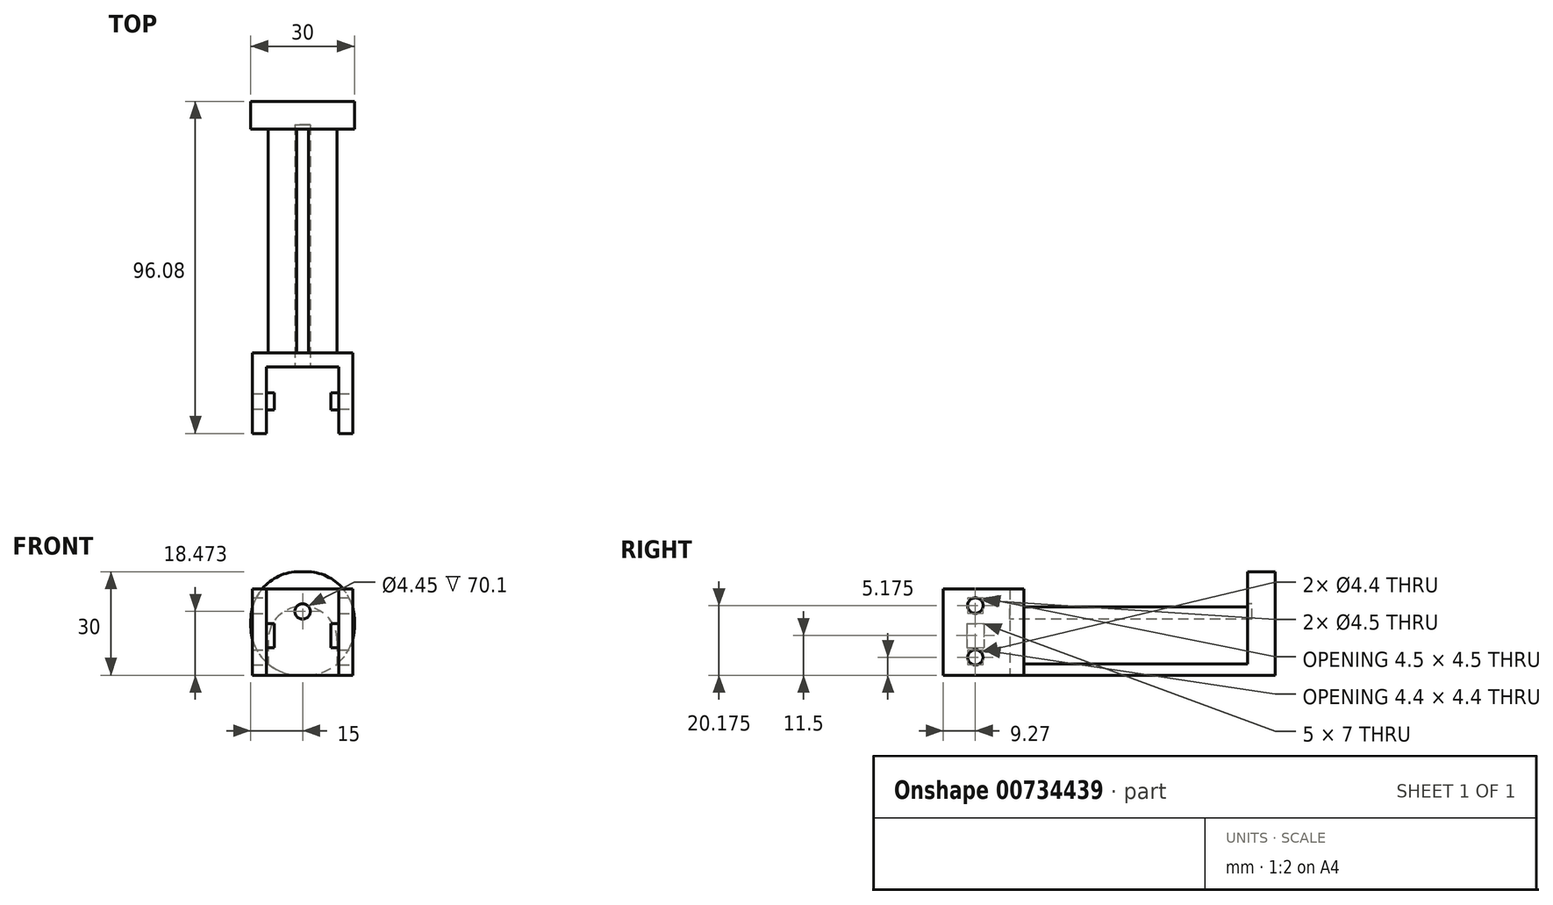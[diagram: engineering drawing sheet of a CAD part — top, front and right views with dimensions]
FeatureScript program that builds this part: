
annotation { "Feature Type Name" : "Feature", "Feature Type Description" : "" }
export const myFeature = defineFeature(function(context is Context, id is Id, definition is map)
    precondition{}
    {
        {
            var Q0;
            Q0=qCreatedBy(makeId("Top.planeOp"),FACE);
            var sketch = newSketch(context, id + "F0", { "sketchPlane" : qUnion([Q0])});
            skLineSegment(sketch, "E0.bottom", {"start": v(13.98, 2.5) * mm, "end": v(8.23, 2.5) * mm});
            skLineSegment(sketch, "E0.top", {"start": v(13.98, -2.5) * mm, "end": v(8.23, -2.5) * mm});
            skLineSegment(sketch, "E0.left", {"start": v(13.98, 2.5) * mm, "end": v(13.98, -2.5) * mm});
            skLineSegment(sketch, "E0.right", {"start": v(8.23, 2.5) * mm, "end": v(8.23, -2.5) * mm});
            skPoint(sketch, "E0.middle", {"position": v(11.1, 0) * mm});
            skPoint(sketch, "E1", {"position": v(10.12, 0) * mm});
            skLineSegment(sketch, "E2.MirrorCS", {"start": v(-13.98, 2.5) * mm, "end": v(-8.23, 2.5) * mm});
            skLineSegment(sketch, "E3.MirrorCS", {"start": v(-13.98, 2.5) * mm, "end": v(-13.98, -2.5) * mm});
            skLineSegment(sketch, "E4.MirrorCS", {"start": v(-13.98, -2.5) * mm, "end": v(-8.23, -2.5) * mm});
            skLineSegment(sketch, "E5.MirrorCS", {"start": v(-8.23, 2.5) * mm, "end": v(-8.23, -2.5) * mm});
            skLineSegment(sketch, "E6.bottom", {"start": v(10.5, -10) * mm, "end": v(-10.5, -10) * mm});
            skLineSegment(sketch, "E6.top", {"start": v(10.5, 10) * mm, "end": v(-10.5, 10) * mm});
            skLineSegment(sketch, "E6.left", {"start": v(10.5, -10) * mm, "end": v(10.5, 10) * mm});
            skLineSegment(sketch, "E6.right", {"start": v(-10.5, -10) * mm, "end": v(-10.5, 10) * mm});
            skPoint(sketch, "E6.middle", {"position": v(0, 0) * mm});
            skLineSegment(sketch, "E7.0", {"start": v(14.5, 14) * mm, "end": v(-14.5, 14) * mm});
            skLineSegment(sketch, "E7.1", {"start": v(14.5, -14) * mm, "end": v(14.5, 14) * mm});
            skLineSegment(sketch, "E7.2", {"start": v(14.5, -14) * mm, "end": v(-14.5, -14) * mm});
            skLineSegment(sketch, "E7.3", {"start": v(-14.5, -14) * mm, "end": v(-14.5, 14) * mm});
            skLineSegment(sketch, "E8", {"start": v(-14.55, -9.27) * mm, "end": v(14.6, -9.27) * mm});
            skLineSegment(sketch, "E9.bottom", {"start": v(10, 14) * mm, "end": v(-10, 14) * mm});
            skLineSegment(sketch, "E9.top", {"start": v(10, 89) * mm, "end": v(-10, 89) * mm});
            skLineSegment(sketch, "E9.left", {"start": v(10, 14) * mm, "end": v(10, 89) * mm});
            skLineSegment(sketch, "E9.right", {"start": v(-10, 14) * mm, "end": v(-10, 89) * mm});
            skPoint(sketch, "E9.middle", {"position": v(0, 51.5) * mm});
            skLineSegment(sketch, "E10.bottom", {"start": v(15, 78.81) * mm, "end": v(-15, 78.81) * mm});
            skLineSegment(sketch, "E10.top", {"start": v(15, 86.81) * mm, "end": v(-15, 86.81) * mm});
            skLineSegment(sketch, "E10.left", {"start": v(15, 78.81) * mm, "end": v(15, 86.81) * mm});
            skLineSegment(sketch, "E10.right", {"start": v(-15, 78.81) * mm, "end": v(-15, 86.81) * mm});
            skPoint(sketch, "E10.middle", {"position": v(0, 82.81) * mm});
            skPoint(sketch, "E10.middle.positionSnap0", {"position": v(0, 89) * mm});
            skPoint(sketch, "E10.centerSnap0", {"position": v(0, 89) * mm});
            skSolve(sketch);
        }
        {
            var Q0;
            {var subQ17=sQuery(id+"F0.wireOp",EDGE,"E0.left");Q0=makeQuery(id+"F0.imprint","IMPRINT",FACE,{"disambiguationData":[TD([[makeQuery(id+"F0.imprint","IMPRINT",EDGE,{"derivedFrom":subQ17}),1.0]])]});}
            var Q1;
            {var subQ0=sQuery(id+"F0.wireOp",EDGE,"E3.MirrorCS");Q1=makeQuery(id+"F0.imprint","IMPRINT",FACE,{"disambiguationData":[TD([[makeQuery(id+"F0.imprint","IMPRINT",EDGE,{"derivedFrom":subQ0}),1.0]])]});}
            var Q2;
            {var subQ0=sQuery(id+"F0.wireOp",EDGE,"E0.left");Q2=makeQuery(id+"F0.imprint","IMPRINT",FACE,{"disambiguationData":[TD([[makeQuery(id+"F0.imprint","IMPRINT",EDGE,{"derivedFrom":subQ0}),-1.0]])]});}
            extrude(context, id + "F1", {"entities" : qUnion([Q0, Q1, Q2]), "depth" : 25 * mm, "offsetDistance" : 25 * mm});
        }
        {
            var Q0;
            {var subQ0=sQuery(id+"F0.wireOp",EDGE,"E5.MirrorCS");Q0=makeQuery(id+"F0.imprint","IMPRINT",FACE,{"disambiguationData":[TD([[makeQuery(id+"F0.imprint","IMPRINT",EDGE,{"derivedFrom":subQ0}),-1.0]])]});}
            var Q1;
            {var subQ0=sQuery(id+"F0.wireOp",EDGE,"E0.right");Q1=makeQuery(id+"F0.imprint","IMPRINT",FACE,{"disambiguationData":[TD([[makeQuery(id+"F0.imprint","IMPRINT",EDGE,{"derivedFrom":subQ0}),1.0]])]});}
            extrude(context, id + "F2", {"entities" : qUnion([Q0, Q1]), "operationType" : NewBodyOperationType.ADD, "depth" : 15 * mm, "offsetDistance" : 25 * mm, "hasSecondDirection" : true, "secondDirectionOppositeDirection" : false, "secondDirectionDepth" : 8 * mm});
        }
        {
            var Q0;
            Q0=makeQuery(id+"F1.opExtrude","SWEPT_FACE",FACE,{"disambiguationData":[OSD([sQuery(id+"F0.wireOp",EDGE,"E7.1")])]});
            var sketch = newSketch(context, id + "F3", { "sketchPlane" : qUnion([Q0])});
            skCircle(sketch, "E11", {"center": v(0, 20.18) * mm, "radius": 2.25 * mm});
            skCircle(sketch, "E12", {"center": v(0, 5.18) * mm, "radius": 2.2 * mm});
            skSolve(sketch);
        }
        {
            var Q0;
            Q0=makeQuery(id+"F3.imprint","IMPRINT",FACE,{"disambiguationData":[TD([[makeQuery(id+"F3.imprint","IMPRINT",EDGE,{"derivedFrom":sQuery(id+"F3.wireOp",EDGE,"E11")}),1.0]])]});
            var Q1;
            Q1=makeQuery(id+"F3.imprint","IMPRINT",FACE,{"disambiguationData":[TD([[makeQuery(id+"F3.imprint","IMPRINT",EDGE,{"derivedFrom":sQuery(id+"F3.wireOp",EDGE,"E12")}),1.0]])]});
            extrude(context, id + "F4", {"entities" : qUnion([Q0, Q1]), "operationType" : NewBodyOperationType.REMOVE, "oppositeDirection" : true, "depth" : 29 * mm, "offsetDistance" : 25 * mm});
        }
        {
            var Q0;
            {var subQ0=sQuery(id+"F0.wireOp",EDGE,"E9.left");var subQ1=sQuery(id+"F0.wireOp",EDGE,"E7.0");var subQ2=makeQuery(id+"F0.imprint","INTERSECT",VERTEX,{"derivedFrom":[subQ1,subQ0]});Q0=makeQuery(id+"F0.imprint","IMPRINT",FACE,{"disambiguationData":[TD([[makeQuery(id+"F0.imprint","IMPRINT",EDGE,{"disambiguationData":[TD([[subQ2,-1.0]])],"derivedFrom":subQ1}),-1.0]])]});}
            extrude(context, id + "F5", {"entities" : qUnion([Q0]), "operationType" : NewBodyOperationType.ADD, "depth" : 20 * mm, "offsetDistance" : 25 * mm});
        }
        {
            var Q0;
            Q0=makeQuery(id+"F5.opExtrude","CAP_EDGE",EDGE,{"disambiguationData":[OSD([sQuery(id+"F0.wireOp",EDGE,"E9.left")])],"isStart":false});
            var Q1;
            Q1=makeQuery(id+"F5.opExtrude","CAP_EDGE",EDGE,{"disambiguationData":[OSD([sQuery(id+"F0.wireOp",EDGE,"E9.right")])],"isStart":false});
            fillet(context, id + "F6", {"entities" : qUnion([Q0, Q1]), "radius" : 10 * mm, "tangentPropagation" : true, "allowEdgeOverflow" : false});
        }
        {
            var Q0;
            {var subQ5=sQuery(id+"F0.wireOp",EDGE,"E10.left");Q0=makeQuery(id+"F0.imprint","IMPRINT",FACE,{"disambiguationData":[TD([[makeQuery(id+"F0.imprint","IMPRINT",EDGE,{"derivedFrom":subQ5}),1.0]])]});}
            var Q1;
            {var subQ0=sQuery(id+"F0.wireOp",EDGE,"E10.bottom");var subQ1=sQuery(id+"F0.wireOp",EDGE,"E9.left");var subQ2=makeQuery(id+"F0.imprint","INTERSECT",VERTEX,{"derivedFrom":[subQ1,subQ0]});Q1=makeQuery(id+"F0.imprint","IMPRINT",FACE,{"disambiguationData":[TD([[makeQuery(id+"F0.imprint","IMPRINT",EDGE,{"disambiguationData":[TD([[subQ2,-1.0]])],"derivedFrom":subQ1}),1.0]])]});}
            var Q2;
            {var subQ5=sQuery(id+"F0.wireOp",EDGE,"E10.right");Q2=makeQuery(id+"F0.imprint","IMPRINT",FACE,{"disambiguationData":[TD([[makeQuery(id+"F0.imprint","IMPRINT",EDGE,{"derivedFrom":subQ5}),-1.0]])]});}
            extrude(context, id + "F7", {"entities" : qUnion([Q0, Q1, Q2]), "operationType" : NewBodyOperationType.ADD, "depth" : 30 * mm, "offsetDistance" : 25 * mm});
        }
        {
            var Q0;
            Q0=makeQuery(id+"F7.opExtrude","CAP_EDGE",EDGE,{"disambiguationData":[OSD([sQuery(id+"F0.wireOp",EDGE,"E10.right")])],"isStart":false});
            var Q1;
            Q1=makeQuery(id+"F7.opExtrude","CAP_EDGE",EDGE,{"disambiguationData":[OSD([sQuery(id+"F0.wireOp",EDGE,"E10.left")])],"isStart":false});
            var Q2;
            Q2=makeQuery(id+"F7.opExtrude","CAP_EDGE",EDGE,{"disambiguationData":[OSD([sQuery(id+"F0.wireOp",EDGE,"E10.left")])],"isStart":true});
            var Q3;
            Q3=makeQuery(id+"F7.opExtrude","CAP_EDGE",EDGE,{"disambiguationData":[OSD([sQuery(id+"F0.wireOp",EDGE,"E10.right")])],"isStart":true});
            fillet(context, id + "F8", {"entities" : qUnion([Q0, Q1, Q2, Q3]), "radius" : 14 * mm, "tangentPropagation" : true, "allowEdgeOverflow" : false});
        }
        {
            var Q0;
            Q0=qCreatedBy(makeId("Front.planeOp"),FACE);
            var sketch = newSketch(context, id + "F9", { "sketchPlane" : qUnion([Q0])});
            skLineSegment(sketch, "E13", {"start": v(23.12, 19.44) * mm, "end": v(-31.22, 19.44) * mm});
            skCircle(sketch, "E14", {"center": v(0, 18.47) * mm, "radius": 2.23 * mm});
            skSolve(sketch);
        }
        {
            var Q0;
            Q0 = qSketchRegion(id + "F9", true);
            extrude(context, id + "F10", {"entities" : qUnion([Q0]), "operationType" : NewBodyOperationType.REMOVE, "oppositeDirection" : true, "depth" : 80.1 * mm, "offsetDistance" : 25 * mm, "hasSecondDirection" : true, "secondDirectionOppositeDirection" : true, "secondDirectionDepth" : 9.7 * mm});
        }
    });
